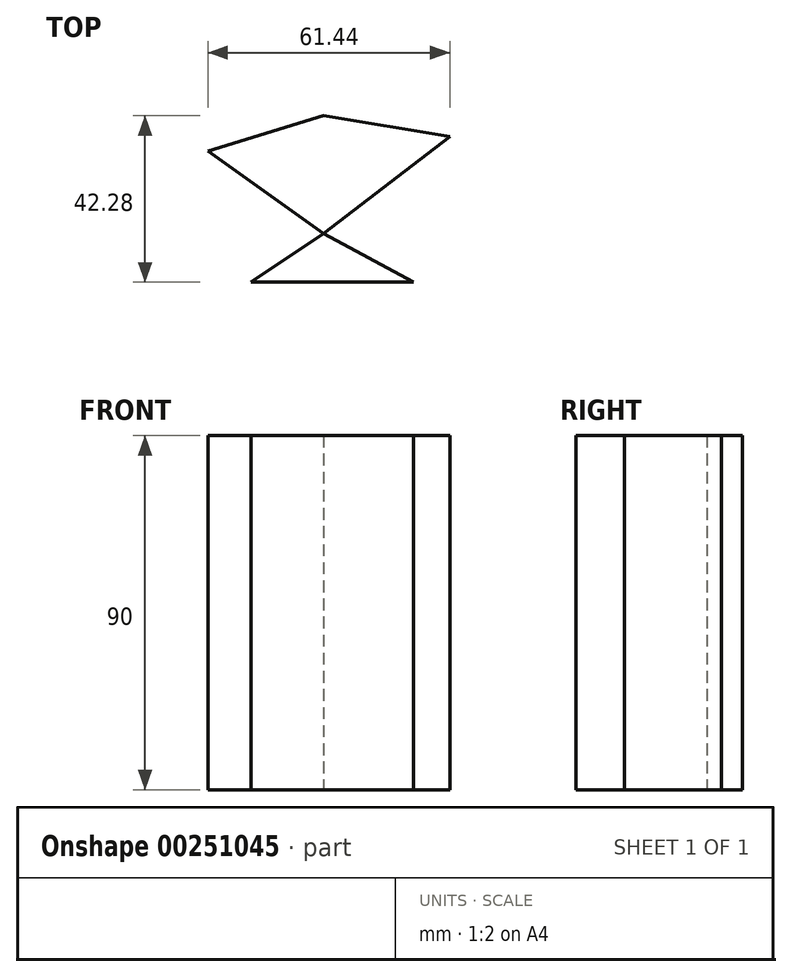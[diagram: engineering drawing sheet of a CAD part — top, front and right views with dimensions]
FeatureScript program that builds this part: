
annotation { "Feature Type Name" : "Feature", "Feature Type Description" : "" }
export const myFeature = defineFeature(function(context is Context, id is Id, definition is map)
    precondition{}
    {
        {
            var Q0;
            Q0=qCreatedBy(makeId("Top.planeOp"),FACE);
            var sketch = newSketch(context, id + "F0", { "sketchPlane" : qUnion([Q0])});
            skLineSegment(sketch, "E0", {"start": v(0, 42.28) * mm, "end": v(0, 0) * mm});
            skLineSegment(sketch, "E1", {"start": v(0, 0) * mm, "end": v(0, 42.28) * mm});
            skLineSegment(sketch, "E2", {"start": v(32.12, 36.98) * mm, "end": v(0, 42.28) * mm});
            skLineSegment(sketch, "E3", {"start": v(0, 12.38) * mm, "end": v(32.12, 36.98) * mm});
            skLineSegment(sketch, "E4", {"start": v(22.84, 0) * mm, "end": v(0, 12.38) * mm});
            skLineSegment(sketch, "E5", {"start": v(0, 0) * mm, "end": v(22.84, 0) * mm});
            skLineSegment(sketch, "E6", {"start": v(-29.32, 33.3) * mm, "end": v(0, 42.28) * mm});
            skLineSegment(sketch, "E7", {"start": v(0, 12.38) * mm, "end": v(-29.32, 33.3) * mm});
            skLineSegment(sketch, "E8", {"start": v(-18.42, 0) * mm, "end": v(0, 12.38) * mm});
            skLineSegment(sketch, "E9", {"start": v(0, 0) * mm, "end": v(-18.42, 0) * mm});
            skSolve(sketch);
        }
        {
            var Q0;
            Q0 = qSketchRegion(id + "F0", true);
            extrude(context, id + "F1", {"entities" : qUnion([Q0]), "depth" : 90 * mm});
        }
    });
